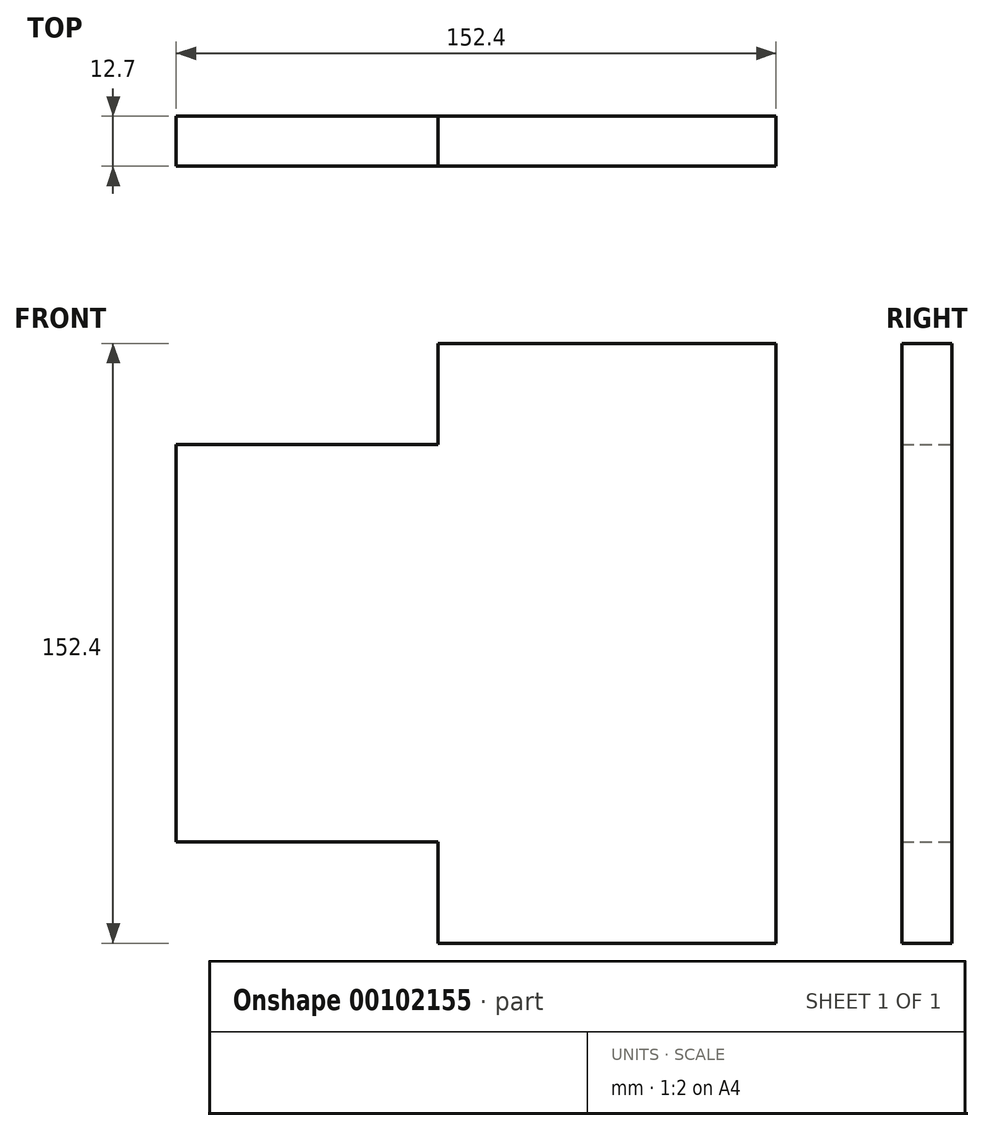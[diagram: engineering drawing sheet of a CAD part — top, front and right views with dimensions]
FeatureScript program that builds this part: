
annotation { "Feature Type Name" : "Feature", "Feature Type Description" : "" }
export const myFeature = defineFeature(function(context is Context, id is Id, definition is map)
    precondition{}
    {
        {
            var Q0;
            Q0=qCreatedBy(makeId("Front.planeOp"),FACE);
            var sketch = newSketch(context, id + "F0", { "sketchPlane" : qUnion([Q0])});
            skLineSegment(sketch, "E0.right", {"start": v(75.91, 0) * mm, "end": v(75.91, 152.4) * mm});
            skLineSegment(sketch, "E1", {"start": v(-76.49, 126.72) * mm, "end": v(-10.03, 126.72) * mm});
            skLineSegment(sketch, "E2", {"start": v(-10.03, 126.72) * mm, "end": v(-10.03, 152.4) * mm});
            skLineSegment(sketch, "E3", {"start": v(-10.03, 152.4) * mm, "end": v(75.91, 152.4) * mm});
            skLineSegment(sketch, "E4", {"start": v(-10.03, 0) * mm, "end": v(-10.03, 25.78) * mm});
            skLineSegment(sketch, "E5", {"start": v(-10.03, 25.78) * mm, "end": v(-76.49, 25.78) * mm});
            skLineSegment(sketch, "E6", {"start": v(-76.49, 25.78) * mm, "end": v(-76.49, 126.72) * mm});
            skLineSegment(sketch, "E7", {"start": v(-10.03, 0) * mm, "end": v(75.91, 0) * mm});
            skSolve(sketch);
        }
        {
            var Q0;
            Q0 = qSketchRegion(id + "F0", true);
            extrude(context, id + "F1", {"entities" : qUnion([Q0]), "depth" : 12.7 * mm});
        }
    });
